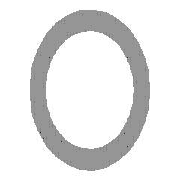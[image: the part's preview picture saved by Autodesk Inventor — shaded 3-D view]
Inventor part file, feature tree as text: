
AUTODESK INVENTOR PART (.ipt)
format: ipt  version: 2017 (Build 210142000, 142)  size: 116,224 bytes
history: native  units: mm (DEFAULTED — no unit token found)
features: other x3, sketch x3, plane x1
ambient origin geometry x8: Origin, YZ Plane, XZ Plane, XY Plane, X Axis, Y Axis, Z Axis, Center Point
bodies: Solid1 (feature_tree), Body (feature_tree)
feature tree (7):
  other  "Driven Length"
  other  "Start plane"
  other  "End plane"
  sketch  "Sketch"  dims[d2=1010.0mm d3=0.0mm d4=-0.0mm d5=1010.0mm d6=90.0deg d7=1010.0mm]
  sketch  "Sketch3"  dims[d0=25.0mm]
  plane  "Work Plane3"
  sketch  "Sketch4"  dims[d1=1.5mm]
